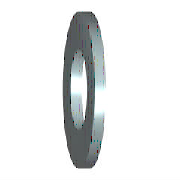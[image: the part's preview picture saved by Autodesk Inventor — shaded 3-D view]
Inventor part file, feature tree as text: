
AUTODESK INVENTOR PART (.ipt)
format: ipt  version: 2015 (Build 190159000, 159)  size: 107,520 bytes
history: native  units: mm (DEFAULTED — no unit token found)
features: extrude x1, other x1, plane x1, sketch x1
ambient origin geometry x7: Origin, YZ Plane, XY Plane, X Axis, Y Axis, Z Axis, Center Point
bodies: Solid1 (feature_tree)
feature tree (4):
  extrude  "Bryła"  Depth=13.0mm
  other  "Work Axis1"
  plane  "Work Plane1"
  sketch  "Szkic"
